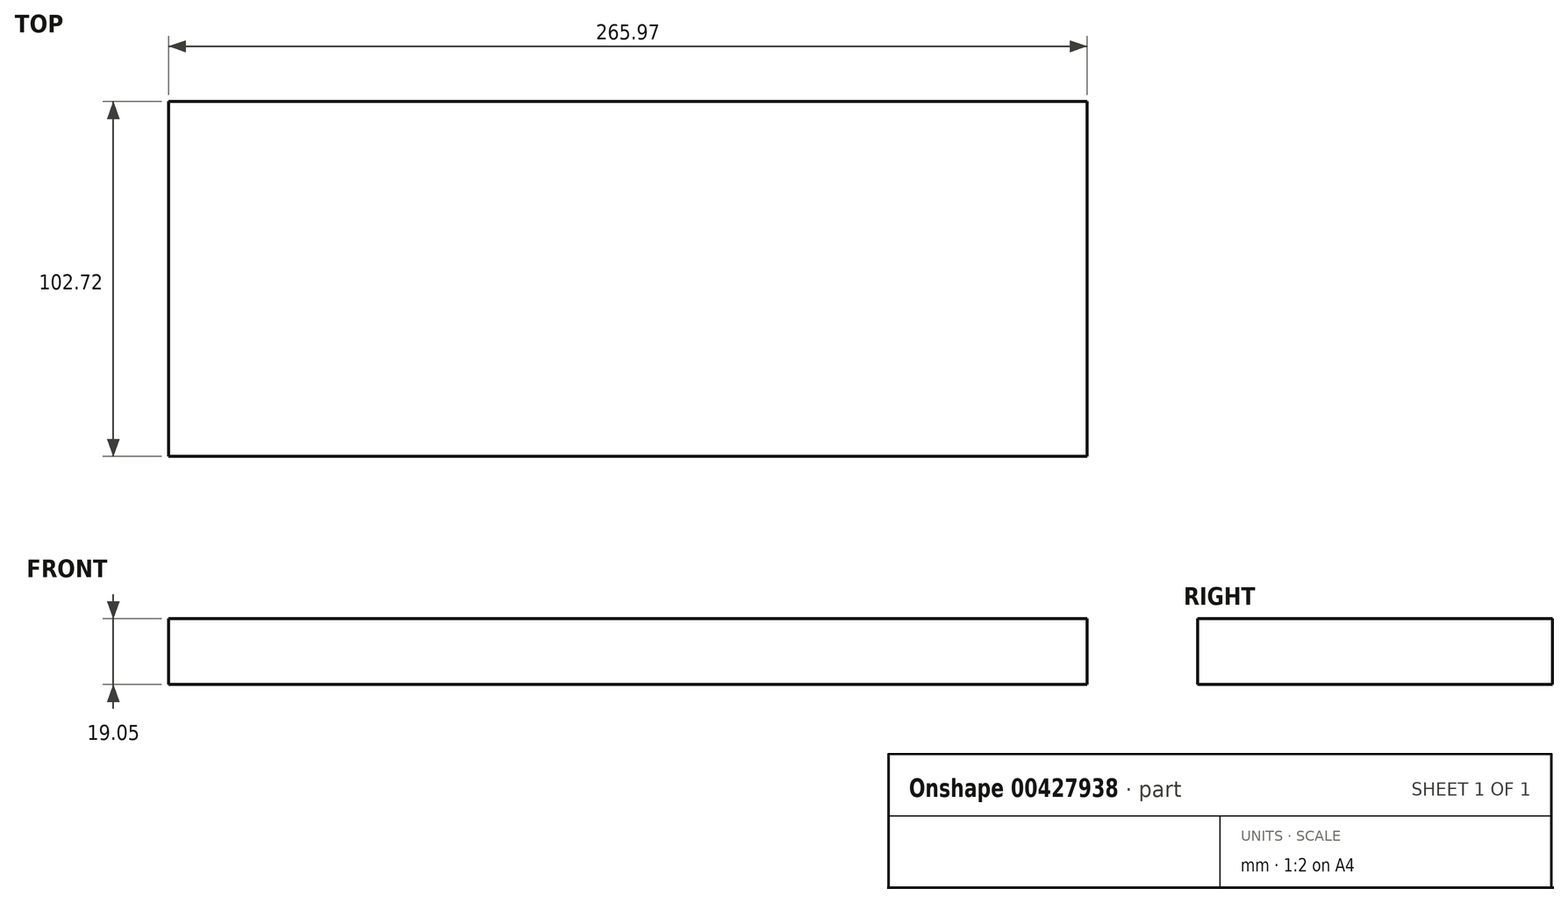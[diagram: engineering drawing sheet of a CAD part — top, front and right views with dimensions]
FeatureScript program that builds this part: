
annotation { "Feature Type Name" : "Feature", "Feature Type Description" : "" }
export const myFeature = defineFeature(function(context is Context, id is Id, definition is map)
    precondition{}
    {
        {
            var Q0;
            Q0=qCreatedBy(makeId("Top.planeOp"),FACE);
            var sketch = newSketch(context, id + "F0", { "sketchPlane" : qUnion([Q0])});
            skLineSegment(sketch, "E0.bottom", {"start": v(-75.53, 73) * mm, "end": v(190.44, 73) * mm});
            skLineSegment(sketch, "E0.top", {"start": v(-75.53, -29.7) * mm, "end": v(190.44, -29.7) * mm});
            skLineSegment(sketch, "E0.left", {"start": v(-75.53, 73) * mm, "end": v(-75.53, -29.7) * mm});
            skLineSegment(sketch, "E0.right", {"start": v(190.44, 73) * mm, "end": v(190.44, -29.7) * mm});
            skSolve(sketch);
        }
        {
            var Q0;
            Q0=makeQuery(id+"F0.imprint","IMPRINT",FACE,{"disambiguationData":[TD([[makeQuery(id+"F0.imprint","IMPRINT",EDGE,{"derivedFrom":sQuery(id+"F0.wireOp",EDGE,"E0.bottom")}),-1.0]])]});
            extrude(context, id + "F1", {"entities" : qUnion([Q0]), "depth" : 19.05 * mm});
        }
    });
